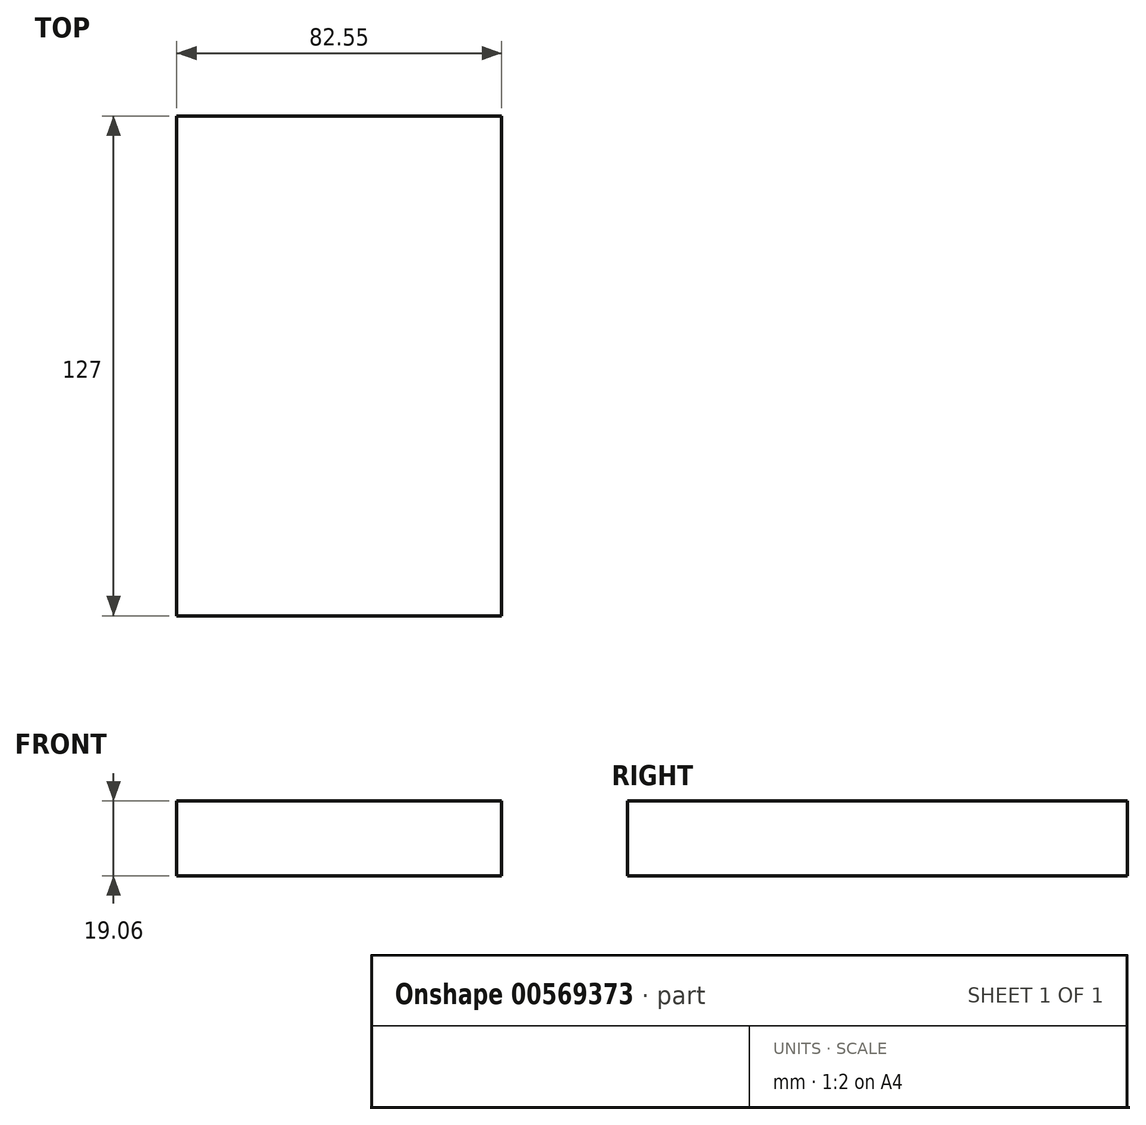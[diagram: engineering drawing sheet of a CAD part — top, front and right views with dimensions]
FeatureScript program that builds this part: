
annotation { "Feature Type Name" : "Feature", "Feature Type Description" : "" }
export const myFeature = defineFeature(function(context is Context, id is Id, definition is map)
    precondition{}
    {
        {
            var Q0;
            Q0=qCreatedBy(makeId("Front.planeOp"),FACE);
            var sketch = newSketch(context, id + "F0", { "sketchPlane" : qUnion([Q0])});
            skLineSegment(sketch, "E0.bottom", {"start": v(-41.28, 9.52) * mm, "end": v(41.28, 9.53) * mm});
            skLineSegment(sketch, "E0.top", {"start": v(-41.28, -9.53) * mm, "end": v(41.28, -9.52) * mm});
            skLineSegment(sketch, "E0.left", {"start": v(-41.28, 9.52) * mm, "end": v(-41.28, -9.53) * mm});
            skLineSegment(sketch, "E0.right", {"start": v(41.28, 9.53) * mm, "end": v(41.28, -9.52) * mm});
            skPoint(sketch, "E0.middle", {"position": v(0, 0) * mm});
            skLineSegment(sketch, "E1.bottom", {"start": v(60.32, 38.1) * mm, "end": v(111.12, 38.1) * mm});
            skLineSegment(sketch, "E1.top", {"start": v(60.32, 66.68) * mm, "end": v(111.12, 66.68) * mm});
            skLineSegment(sketch, "E1.left", {"start": v(60.33, 38.1) * mm, "end": v(60.32, 66.67) * mm});
            skLineSegment(sketch, "E1.right", {"start": v(111.12, 38.1) * mm, "end": v(111.12, 66.67) * mm});
            skPoint(sketch, "E1.middle", {"position": v(85.72, 52.39) * mm});
            skLineSegment(sketch, "E2", {"start": v(41.28, 9.53) * mm, "end": v(41.28, 27) * mm});
            skArc(sketch, "E3", {"start": v(41.28, 27) * mm, "mid": v(46.01, 38.32) * mm, "end": v(57.4, 42.88) * mm});
            skLineSegment(sketch, "E4", {"start": v(57.4, 42.88) * mm, "end": v(85.73, 42.88) * mm});
            skLineSegment(sketch, "E5.0", {"start": v(57.51, 61.93) * mm, "end": v(85.72, 61.93) * mm});
            skArc(sketch, "E5.1", {"start": v(22.23, 27) * mm, "mid": v(32.58, 51.83) * mm, "end": v(57.51, 61.93) * mm});
            skLineSegment(sketch, "E5.2", {"start": v(22.23, 9.53) * mm, "end": v(22.23, 27) * mm});
            skLineSegment(sketch, "E6", {"start": v(85.72, 38.1) * mm, "end": v(85.72, 66.68) * mm});
            skSolve(sketch);
        }
        {
            var Q0;
            Q0=makeQuery(id+"F0.imprint","IMPRINT",FACE,{"disambiguationData":[TD([[makeQuery(id+"F0.imprint","IMPRINT",EDGE,{"derivedFrom":sQuery(id+"F0.wireOp",EDGE,"E0.top")}),1.0]])]});
            extrude(context, id + "F1", {"entities" : qUnion([Q0]), "endBound" : BoundingType.SYMMETRIC, "depth" : 127 * mm, "offsetDistance" : 25.4 * mm});
        }
    });
